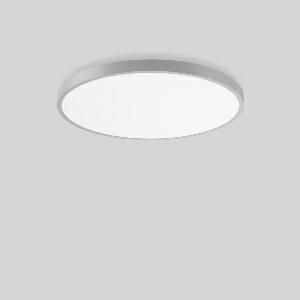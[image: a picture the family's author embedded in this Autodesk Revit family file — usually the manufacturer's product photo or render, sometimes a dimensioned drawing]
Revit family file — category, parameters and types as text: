
# Revit family: triona_round_a_312388_004_730_06b1
name_source: partatom
category: Lighting Fixtures
units: mm (PartAtom-declared; Revit-internal decimal feet)

## family parameters
Cut with Voids When Loaded = No
Host = Face
Light Source = No
Part Type = Normal
Room Calculation Point = No
Round Connector Dimension = Use Diameter
Shared = No

## types (1)
- TRIONA round A (1 x LED Modul 830, 12400 lm, 3000)
    Apparent Load = 133 VA
    CIE Flux Codes = 49 80 96 71 100
    Color Rendering = 80
    Color Temperature = 3000
    Default Elevation = 1800 mm
    Description = Series: TRIONA round
Decorative round LED surface-mounted luminaire. Flat, seamless frame: aluminium extrusion profile, powder coated. Cover made of sheet steel, powder-coated. Direct light emission through a diffuser plastic opal. Indirect light emission through a flush diffuser made of satin-finish plastic. Lightguide and diffuser made of non-yellowing plastic (PMMA). Lateral light emission (RZB SIDELITE technology) for above-average homogeneous light distribution. Direct 70%, indirect 30% light emission. Suitable for Ceiling mounting, Wall (surface). Tool-free mounting via bayonet connection. Electronic ballast included. Very easy installation thanks to Plug+Play connection. With Casambi smart+free Bluetooth control for wireless network and operation using Android / iOS devices, free app available for download. 
Colour: silver, matt (approx. RAL 9006)
Diameter: 845 mm
Height: 88 mm
Lamp: LED
Socket: without socket
Colour temperature: 3000K
Colour rendering index (CRI): 80
System power: 133 W
Rated luminous flux: 12400 lm
Luminous efficiency: 93 lm/W
Control gear: Dimmable Bluetooth converter
Protection class: I
Type of protection: IP 20
    Height = 88 mm
    Lamp = 1 x LED Modul 830
    Lamp Light Flux = 12400 lm
    Lamp count = 1
    Length = 845 mm
    Lifetime = 50000 h
    Luminous efficacy = 93 lm/W
    Manufacturer = RZB
    ModVariant = No
    Model = 312388.004.730
    Mounting Place = Ceiling
    Mounting Type = Surface mounted
    Number of Poles = 1
    OnlyDefault = Yes
    Power Factor = 1
    Product Name = TRIONA round A
    Product group = Surface mounted modular luminaires
    ProductGroupID = 306
    Protection Class = Protection class I
    Protection Degree = IP 20
    RLX_Detail_Level = 1
    RLX_Emergency_Light_Flux = 0 lm
    RLX_Emergency_Type = 0
    RLX_Emergency_Type_DB = No
    RlxData = <blob elided: 42185 chars, md5=ed22e9b8>
    Socket = socket
    Standby Power = 0 W
    System Light Flux = 12400 lm
    System Power = 133 W
    Type Comments = Product without accessories
    Type Image = 312388.004.jpg
    URL = http://relux.com
    VarID = ---
    Voltage = 230 V
    Voltage Range = 220-240 V
    Weight = 0.00 kg
    Width = 0 mm  [stored 0 ft]

note: [stored X ft] marks values corroborated as IEEE doubles in the binary element streams (Revit-internal decimal feet)

## geometry (parser evidence)
native form markers: Blend x4, Sweep x13
no freeform markers — native parametric forms only
